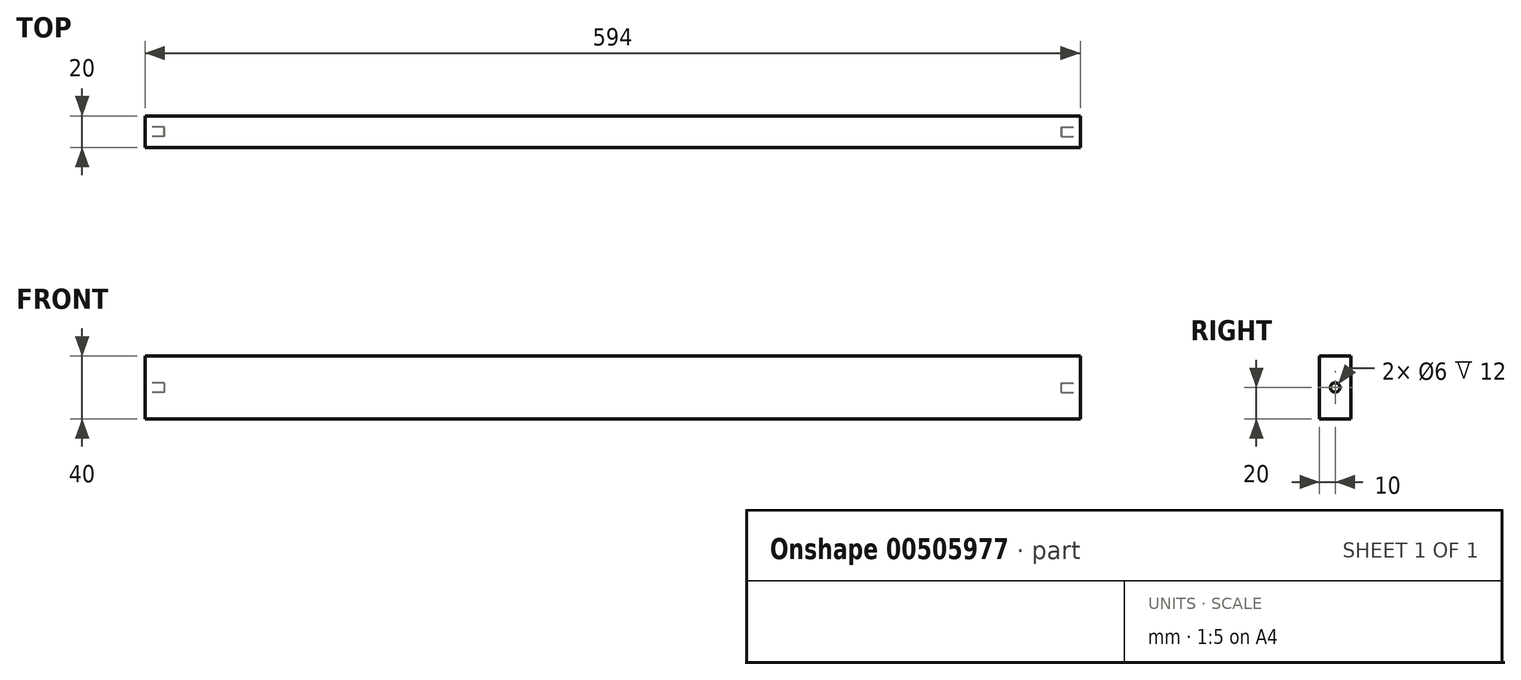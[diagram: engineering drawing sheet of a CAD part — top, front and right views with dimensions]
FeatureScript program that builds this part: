
annotation { "Feature Type Name" : "Feature", "Feature Type Description" : "" }
export const myFeature = defineFeature(function(context is Context, id is Id, definition is map)
    precondition{}
    {
        {
            var Q0;
            Q0=qCreatedBy(makeId("Front.planeOp"),FACE);
            var sketch = newSketch(context, id + "F0", { "sketchPlane" : qUnion([Q0])});
            skLineSegment(sketch, "E0.bottom", {"start": v(-130.73, 40) * mm, "end": v(463.27, 40) * mm});
            skLineSegment(sketch, "E0.top", {"start": v(-130.73, 0) * mm, "end": v(463.27, 0) * mm});
            skLineSegment(sketch, "E0.left", {"start": v(-130.73, 40) * mm, "end": v(-130.73, 0) * mm});
            skLineSegment(sketch, "E0.right", {"start": v(463.27, 40) * mm, "end": v(463.27, 0) * mm});
            skSolve(sketch);
        }
        {
            var Q0;
            Q0=makeQuery(id+"F0.imprint","IMPRINT",FACE,{"disambiguationData":[TD([[makeQuery(id+"F0.imprint","IMPRINT",EDGE,{"derivedFrom":sQuery(id+"F0.wireOp",EDGE,"E0.bottom")}),-1.0]])]});
            extrude(context, id + "F1", {"entities" : qUnion([Q0]), "depth" : 20 * mm, "offsetDistance" : 25 * mm});
        }
        {
            var Q0;
            Q0=makeQuery(id+"F1.opExtrude","SWEPT_FACE",FACE,{"disambiguationData":[OSD([sQuery(id+"F0.wireOp",EDGE,"E0.right")])]});
            var sketch = newSketch(context, id + "F2", { "sketchPlane" : qUnion([Q0])});
            skCircle(sketch, "E1", {"center": v(-10, 20) * mm, "radius": 3 * mm});
            skSolve(sketch);
        }
        {
            var Q0;
            Q0 = qSketchRegion(id + "F2", true);
            extrude(context, id + "F3", {"entities" : qUnion([Q0]), "operationType" : NewBodyOperationType.REMOVE, "oppositeDirection" : true, "depth" : 12 * mm, "offsetDistance" : 25 * mm});
        }
        {
            var Q0;
            Q0=makeQuery(id+"F1.opExtrude","SWEPT_FACE",FACE,{"disambiguationData":[OSD([sQuery(id+"F0.wireOp",EDGE,"E0.left")])]});
            var sketch = newSketch(context, id + "F4", { "sketchPlane" : qUnion([Q0])});
            skCircle(sketch, "E2", {"center": v(10, 20) * mm, "radius": 3 * mm});
            skSolve(sketch);
        }
        {
            var Q0;
            Q0 = qSketchRegion(id + "F4", true);
            extrude(context, id + "F5", {"entities" : qUnion([Q0]), "operationType" : NewBodyOperationType.REMOVE, "oppositeDirection" : true, "depth" : 12 * mm, "offsetDistance" : 25 * mm});
        }
    });
